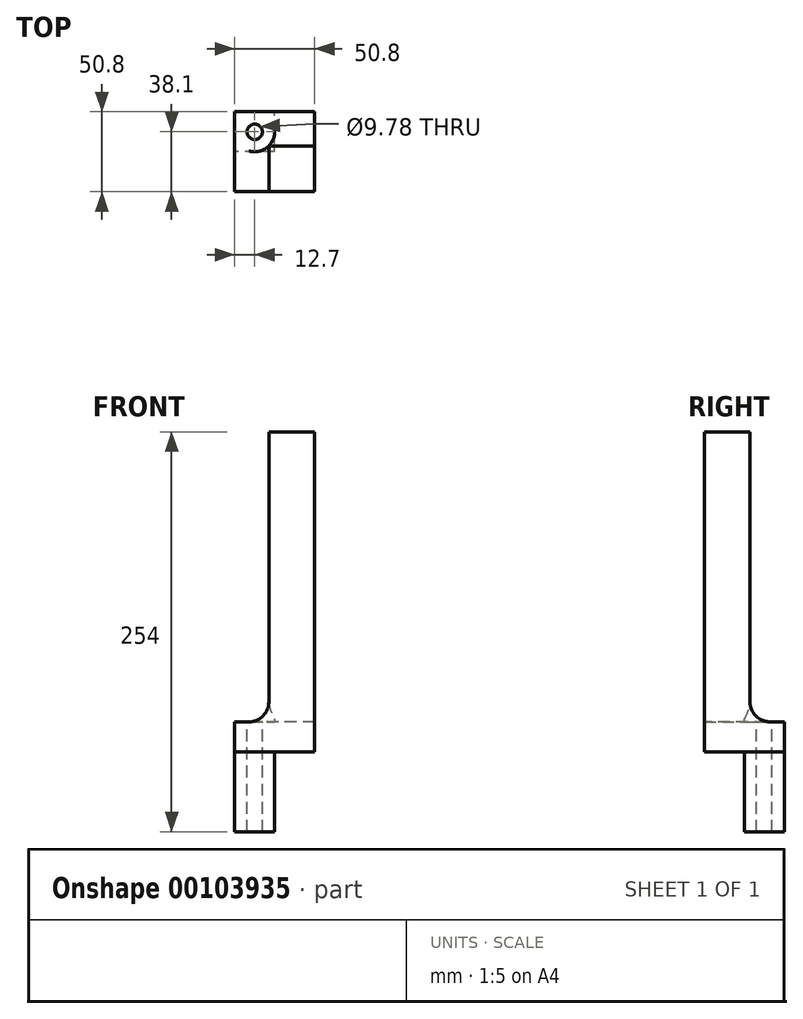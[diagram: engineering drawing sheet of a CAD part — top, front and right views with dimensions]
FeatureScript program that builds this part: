
annotation { "Feature Type Name" : "Feature", "Feature Type Description" : "" }
export const myFeature = defineFeature(function(context is Context, id is Id, definition is map)
    precondition{}
    {
        {
            var Q0;
            Q0=qCreatedBy(makeId("Top.planeOp"),FACE);
            var sketch = newSketch(context, id + "F0", { "sketchPlane" : qUnion([Q0])});
            skLineSegment(sketch, "E0.bottom", {"start": v(0, 0) * mm, "end": v(-50.8, 0) * mm});
            skLineSegment(sketch, "E0.top", {"start": v(0, 50.8) * mm, "end": v(-50.8, 50.8) * mm});
            skLineSegment(sketch, "E0.left", {"start": v(0, 0) * mm, "end": v(0, 50.8) * mm});
            skLineSegment(sketch, "E0.right", {"start": v(-50.8, 0) * mm, "end": v(-50.8, 50.8) * mm});
            skSolve(sketch);
        }
        {
            var Q0;
            Q0=qSketchRegion(id+"F0",true);
            extrude(context, id + "F1", {"entities" : qUnion([Q0]), "depth" : 254 * mm});
        }
        {
            var Q0;
            Q0=makeQuery(id+"F1.opExtrude","SWEPT_FACE",FACE,{"disambiguationData":[OSD([sQuery(id+"F0.wireOp",EDGE,"E0.right")])]});
            var sketch = newSketch(context, id + "F2", { "sketchPlane" : qUnion([Q0])});
            skLineSegment(sketch, "E1", {"start": v(-50.8, 69.85) * mm, "end": v(-41.82, 69.85) * mm});
            skArc(sketch, "E2", {"start": v(-41.82, 69.85) * mm, "mid": v(-32.84, 73.57) * mm, "end": v(-29.12, 82.55) * mm});
            skLineSegment(sketch, "E3", {"start": v(-29.12, 82.55) * mm, "end": v(-29.12, 254) * mm});
            skLineSegment(sketch, "E4", {"start": v(-29.12, 254) * mm, "end": v(-50.8, 254) * mm});
            skLineSegment(sketch, "E5", {"start": v(-50.8, 254) * mm, "end": v(-50.8, 69.85) * mm});
            skSolve(sketch);
        }
        {
            var Q0;
            Q0=qSketchRegion(id+"F2",true);
            extrude(context, id + "F3", {"entities" : qUnion([Q0]), "operationType" : NewBodyOperationType.REMOVE, "endBound" : BoundingType.THROUGH_ALL, "oppositeDirection" : true, "depth" : 25.4 * mm});
        }
        {
            var Q0;
            Q0=makeQuery(id+"F1.opExtrude","SWEPT_FACE",FACE,{"disambiguationData":[OSD([sQuery(id+"F0.wireOp",EDGE,"E0.top")])]});
            var sketch = newSketch(context, id + "F4", { "sketchPlane" : qUnion([Q0])});
            skLineSegment(sketch, "E6", {"start": v(41.82, 69.85) * mm, "end": v(50.8, 69.85) * mm});
            skLineSegment(sketch, "E7", {"start": v(50.8, 69.85) * mm, "end": v(50.8, 254) * mm});
            skLineSegment(sketch, "E8", {"start": v(50.8, 254) * mm, "end": v(29.12, 254) * mm});
            skLineSegment(sketch, "E9", {"start": v(29.12, 254) * mm, "end": v(29.12, 82.55) * mm});
            skArc(sketch, "E10", {"start": v(29.12, 82.55) * mm, "mid": v(32.84, 73.57) * mm, "end": v(41.82, 69.85) * mm});
            skSolve(sketch);
        }
        {
            var Q0;
            Q0=qSketchRegion(id+"F4",true);
            extrude(context, id + "F5", {"entities" : qUnion([Q0]), "operationType" : NewBodyOperationType.REMOVE, "endBound" : BoundingType.THROUGH_ALL, "oppositeDirection" : true, "depth" : 25.4 * mm});
        }
        {
            var Q0;
            Q0=makeQuery(id+"F5.boolean.opBoolean","MERGE",FACE,{"derivedFrom":[makeQuery(id+"F3.boolean.opBoolean","COPY",FACE,{"derivedFrom":makeQuery(id+"F3.opExtrude","SWEPT_FACE",FACE,{"disambiguationData":[OSD([sQuery(id+"F2.wireOp",EDGE,"E1")])]})}),makeQuery(id+"F5.opExtrude","SWEPT_FACE",FACE,{"disambiguationData":[OSD([sQuery(id+"F4.wireOp",EDGE,"E6")])]})]});
            var sketch = newSketch(context, id + "F6", { "sketchPlane" : qUnion([Q0])});
            skCircle(sketch, "E11", {"center": v(-38.1, 38.1) * mm, "radius": 12.7 * mm});
            skSolve(sketch);
        }
        {
            var Q0;
            Q0=qSketchRegion(id+"F6",true);
            extrude(context, id + "F7", {"entities" : qUnion([Q0]), "operationType" : NewBodyOperationType.REMOVE, "depth" : 25.4 * mm});
        }
        {
            var Q0;
            Q0=makeQuery(id+"F1.opExtrude","CAP_FACE",FACE,{"disambiguationData":[OSD([sQuery(id+"F0.wireOp",EDGE,"E0.bottom"),sQuery(id+"F0.wireOp",EDGE,"E0.top"),sQuery(id+"F0.wireOp",EDGE,"E0.left"),sQuery(id+"F0.wireOp",EDGE,"E0.right")])],"isStart":true});
            var sketch = newSketch(context, id + "F8", { "sketchPlane" : qUnion([Q0])});
            skLineSegment(sketch, "E12.bottom", {"start": v(0, 0) * mm, "end": v(-25.4, 0) * mm});
            skLineSegment(sketch, "E12.top", {"start": v(0, -50.8) * mm, "end": v(-25.4, -50.8) * mm});
            skLineSegment(sketch, "E12.left", {"start": v(0, 0) * mm, "end": v(0, -50.8) * mm});
            skLineSegment(sketch, "E12.right", {"start": v(-25.4, -25.4) * mm, "end": v(-25.4, -50.8) * mm});
            skLineSegment(sketch, "E13.bottom", {"start": v(0, 0) * mm, "end": v(-50.8, 0) * mm});
            skLineSegment(sketch, "E13.top", {"start": v(-25.4, -25.4) * mm, "end": v(-50.8, -25.4) * mm});
            skLineSegment(sketch, "E13.left", {"start": v(0, 0) * mm, "end": v(0, -25.4) * mm});
            skLineSegment(sketch, "E13.right", {"start": v(-50.8, 0) * mm, "end": v(-50.8, -25.4) * mm});
            skSolve(sketch);
        }
        {
            var Q0;
            Q0 = qSketchRegion(id + "F8", true);
            extrude(context, id + "F9", {"entities" : qUnion([Q0]), "operationType" : NewBodyOperationType.REMOVE, "oppositeDirection" : true, "depth" : 50.8 * mm});
        }
        {
            var Q0;
            Q0=makeQuery(id+"F7.boolean.opBoolean","MERGE",FACE,{"derivedFrom":[makeQuery(id+"F5.boolean.opBoolean","MERGE",FACE,{"derivedFrom":[makeQuery(id+"F3.boolean.opBoolean","COPY",FACE,{"derivedFrom":makeQuery(id+"F3.opExtrude","SWEPT_FACE",FACE,{"disambiguationData":[OSD([sQuery(id+"F2.wireOp",EDGE,"E1")])]})}),makeQuery(id+"F5.opExtrude","SWEPT_FACE",FACE,{"disambiguationData":[OSD([sQuery(id+"F4.wireOp",EDGE,"E6")])]})]}),makeQuery(id+"F7.opExtrude","CAP_FACE",FACE,{"disambiguationData":[OSD([sQuery(id+"F6.wireOp",EDGE,"E11")])],"isStart":true})]});
            var sketch = newSketch(context, id + "F10", { "sketchPlane" : qUnion([Q0])});
            skCircle(sketch, "E14", {"center": v(-38.1, 38.1) * mm, "radius": 4.89 * mm});
            skSolve(sketch);
        }
        {
            var Q0;
            Q0 = qSketchRegion(id + "F10", true);
            extrude(context, id + "F11", {"entities" : qUnion([Q0]), "operationType" : NewBodyOperationType.REMOVE, "endBound" : BoundingType.THROUGH_ALL, "oppositeDirection" : true, "depth" : 25.4 * mm});
        }
    });
